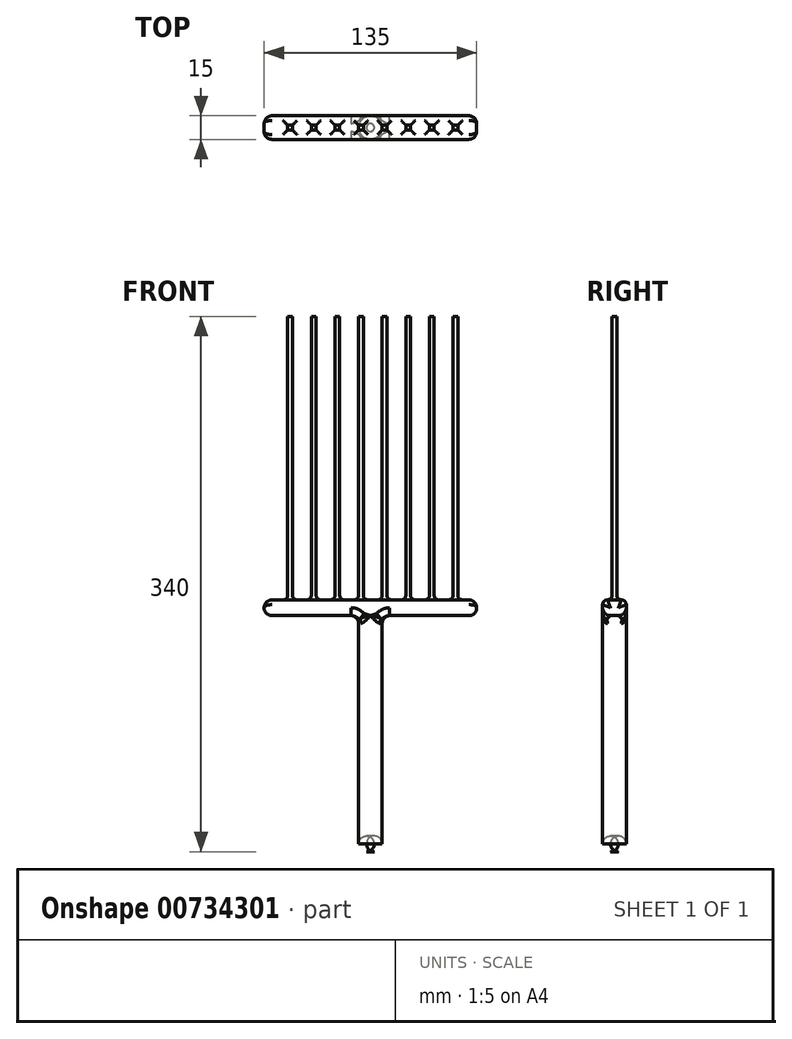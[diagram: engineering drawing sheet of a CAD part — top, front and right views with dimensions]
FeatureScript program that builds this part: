
annotation { "Feature Type Name" : "Feature", "Feature Type Description" : "" }
export const myFeature = defineFeature(function(context is Context, id is Id, definition is map)
    precondition{}
    {
        {
            var Q0;
            Q0=qCreatedBy(makeId("Top.planeOp"),FACE);
            var sketch = newSketch(context, id + "F0", { "sketchPlane" : qUnion([Q0])});
            skCircle(sketch, "E0", {"center": v(0, 0) * mm, "radius": 7.5 * mm});
            skSolve(sketch);
        }
        {
            var Q0;
            Q0 = qSketchRegion(id + "F0", true);
            extrude(context, id + "F1", {"entities" : qUnion([Q0]), "depth" : 150 * mm, "offsetDistance" : 25 * mm});
        }
        {
            var Q0;
            Q0=makeQuery(id+"F1.opExtrude","CAP_FACE",FACE,{"disambiguationData":[OSD([sQuery(id+"F0.wireOp",EDGE,"E0")])],"isStart":false});
            var sketch = newSketch(context, id + "F2", { "sketchPlane" : qUnion([Q0])});
            skLineSegment(sketch, "E1.bottom", {"start": v(67.5, -7.5) * mm, "end": v(-67.5, -7.5) * mm});
            skLineSegment(sketch, "E1.top", {"start": v(67.5, 7.5) * mm, "end": v(-67.5, 7.5) * mm});
            skLineSegment(sketch, "E1.left", {"start": v(67.5, -7.5) * mm, "end": v(67.5, 7.5) * mm});
            skLineSegment(sketch, "E1.right", {"start": v(-67.5, -7.5) * mm, "end": v(-67.5, 7.5) * mm});
            skPoint(sketch, "E1.middle", {"position": v(0, 0) * mm});
            skSolve(sketch);
        }
        {
            var Q0;
            Q0 = qSketchRegion(id + "F2", true);
            extrude(context, id + "F3", {"entities" : qUnion([Q0]), "operationType" : NewBodyOperationType.ADD, "depth" : 10 * mm, "offsetDistance" : 25 * mm});
        }
        {
            var Q0;
            Q0=makeQuery(id+"F3.opExtrude","CAP_FACE",FACE,{"disambiguationData":[OSD([sQuery(id+"F2.wireOp",EDGE,"E1.bottom"),sQuery(id+"F2.wireOp",EDGE,"E1.top"),sQuery(id+"F2.wireOp",EDGE,"E1.left"),sQuery(id+"F2.wireOp",EDGE,"E1.right")])],"isStart":false});
            var sketch = newSketch(context, id + "F4", { "sketchPlane" : qUnion([Q0])});
            skLineSegment(sketch, "E2.bottom", {"start": v(-64.5, -1.5) * mm, "end": v(-67.5, -1.5) * mm});
            skLineSegment(sketch, "E2.top", {"start": v(-64.5, 1.5) * mm, "end": v(-67.5, 1.5) * mm});
            skLineSegment(sketch, "E2.left", {"start": v(-64.5, -1.5) * mm, "end": v(-64.5, 1.5) * mm});
            skLineSegment(sketch, "E2.right", {"start": v(-67.5, -1.5) * mm, "end": v(-67.5, 1.5) * mm});
            skPoint(sketch, "E2.middle", {"position": v(-66, 0) * mm});
            skLineSegment(sketch, "E3.bottom", {"start": v(-49.5, -1.5) * mm, "end": v(-52.5, -1.5) * mm});
            skLineSegment(sketch, "E3.top", {"start": v(-49.5, 1.5) * mm, "end": v(-52.5, 1.5) * mm});
            skLineSegment(sketch, "E3.left", {"start": v(-49.5, -1.5) * mm, "end": v(-49.5, 1.5) * mm});
            skLineSegment(sketch, "E3.right", {"start": v(-52.5, -1.5) * mm, "end": v(-52.5, 1.5) * mm});
            skPoint(sketch, "E3.middle", {"position": v(-51, 0) * mm});
            skLineSegment(sketch, "E4.bottom", {"start": v(-34.5, -1.5) * mm, "end": v(-37.5, -1.5) * mm});
            skLineSegment(sketch, "E4.top", {"start": v(-34.5, 1.5) * mm, "end": v(-37.5, 1.5) * mm});
            skLineSegment(sketch, "E4.left", {"start": v(-34.5, -1.5) * mm, "end": v(-34.5, 1.5) * mm});
            skLineSegment(sketch, "E4.right", {"start": v(-37.5, -1.5) * mm, "end": v(-37.5, 1.5) * mm});
            skPoint(sketch, "E4.middle", {"position": v(-36, 0) * mm});
            skLineSegment(sketch, "E5.bottom", {"start": v(-19.5, -1.5) * mm, "end": v(-22.5, -1.5) * mm});
            skLineSegment(sketch, "E5.top", {"start": v(-19.5, 1.5) * mm, "end": v(-22.5, 1.5) * mm});
            skLineSegment(sketch, "E5.left", {"start": v(-19.5, -1.5) * mm, "end": v(-19.5, 1.5) * mm});
            skLineSegment(sketch, "E5.right", {"start": v(-22.5, -1.5) * mm, "end": v(-22.5, 1.5) * mm});
            skPoint(sketch, "E5.middle", {"position": v(-21, 0) * mm});
            skLineSegment(sketch, "E6.bottom", {"start": v(-4.5, -1.5) * mm, "end": v(-7.5, -1.5) * mm});
            skLineSegment(sketch, "E6.top", {"start": v(-4.5, 1.5) * mm, "end": v(-7.5, 1.5) * mm});
            skLineSegment(sketch, "E6.left", {"start": v(-4.5, -1.5) * mm, "end": v(-4.5, 1.5) * mm});
            skLineSegment(sketch, "E6.right", {"start": v(-7.5, -1.5) * mm, "end": v(-7.5, 1.5) * mm});
            skPoint(sketch, "E6.middle", {"position": v(-6, 0) * mm});
            skLineSegment(sketch, "E7.bottom", {"start": v(10.5, -1.5) * mm, "end": v(7.5, -1.5) * mm});
            skLineSegment(sketch, "E7.top", {"start": v(10.5, 1.5) * mm, "end": v(7.5, 1.5) * mm});
            skLineSegment(sketch, "E7.left", {"start": v(10.5, -1.5) * mm, "end": v(10.5, 1.5) * mm});
            skLineSegment(sketch, "E7.right", {"start": v(7.5, -1.5) * mm, "end": v(7.5, 1.5) * mm});
            skPoint(sketch, "E7.middle", {"position": v(9, 0) * mm});
            skLineSegment(sketch, "E8.bottom", {"start": v(25.5, -1.5) * mm, "end": v(22.5, -1.5) * mm});
            skLineSegment(sketch, "E8.top", {"start": v(25.5, 1.5) * mm, "end": v(22.5, 1.5) * mm});
            skLineSegment(sketch, "E8.left", {"start": v(25.5, -1.5) * mm, "end": v(25.5, 1.5) * mm});
            skLineSegment(sketch, "E8.right", {"start": v(22.5, -1.5) * mm, "end": v(22.5, 1.5) * mm});
            skPoint(sketch, "E8.middle", {"position": v(24, 0) * mm});
            skLineSegment(sketch, "E9.bottom", {"start": v(40.5, -1.5) * mm, "end": v(37.5, -1.5) * mm});
            skLineSegment(sketch, "E9.top", {"start": v(40.5, 1.5) * mm, "end": v(37.5, 1.5) * mm});
            skLineSegment(sketch, "E9.left", {"start": v(40.5, -1.5) * mm, "end": v(40.5, 1.5) * mm});
            skLineSegment(sketch, "E9.right", {"start": v(37.5, -1.5) * mm, "end": v(37.5, 1.5) * mm});
            skPoint(sketch, "E9.middle", {"position": v(39, 0) * mm});
            skLineSegment(sketch, "E10.bottom", {"start": v(55.5, -1.5) * mm, "end": v(52.5, -1.5) * mm});
            skLineSegment(sketch, "E10.top", {"start": v(55.5, 1.5) * mm, "end": v(52.5, 1.5) * mm});
            skLineSegment(sketch, "E10.left", {"start": v(55.5, -1.5) * mm, "end": v(55.5, 1.5) * mm});
            skLineSegment(sketch, "E10.right", {"start": v(52.5, -1.5) * mm, "end": v(52.5, 1.5) * mm});
            skPoint(sketch, "E10.middle", {"position": v(54, 0) * mm});
            skLineSegment(sketch, "E11.bottom", {"start": v(67.5, -1.5) * mm, "end": v(64.5, -1.5) * mm});
            skLineSegment(sketch, "E11.top", {"start": v(67.5, 1.5) * mm, "end": v(64.5, 1.5) * mm});
            skLineSegment(sketch, "E11.left", {"start": v(67.5, -1.5) * mm, "end": v(67.5, 1.5) * mm});
            skLineSegment(sketch, "E11.right", {"start": v(64.5, -1.5) * mm, "end": v(64.5, 1.5) * mm});
            skPoint(sketch, "E11.middle", {"position": v(66, 0) * mm});
            skSolve(sketch);
        }
        {
            var Q0;
            Q0 = qSketchRegion(id + "F4", true);
            extrude(context, id + "F5", {"entities" : qUnion([Q0]), "operationType" : NewBodyOperationType.ADD, "depth" : 180 * mm, "offsetDistance" : 25 * mm});
        }
        {
            var Q0;
            Q0=makeQuery(id+"F1.opExtrude","CAP_EDGE",EDGE,{"disambiguationData":[OSD([sQuery(id+"F0.wireOp",EDGE,"E0")])],"isStart":true});
            var Q1;
            Q1=makeQuery(id+"F1.opExtrude","SWEPT_FACE",FACE,{"disambiguationData":[OSD([sQuery(id+"F0.wireOp",EDGE,"E0")])]});
            fillet(context, id + "F6", {"entities" : qUnion([Q0, Q1]), "radius" : 5 * mm, "tangentPropagation" : true, "allowEdgeOverflow" : false});
        }
        {
            var Q0;
            {var subQ0=sQuery(id+"F2.wireOp",EDGE,"E1.top");var subQ1=sQuery(id+"F2.wireOp",EDGE,"E1.right");var subQ2=sQuery(id+"F2.wireOp",EDGE,"E1.bottom");var subQ3=makeQuery(id+"F3.opExtrude","CAP_FACE",FACE,{"disambiguationData":[OSD([subQ2,subQ0,sQuery(id+"F2.wireOp",EDGE,"E1.left"),subQ1])],"isStart":true});Q0=makeQuery(id+"F3.boolean.opBoolean","SPLIT",FACE,{"disambiguationData":[TD([makeQuery(id+"F3.opExtrude","SWEPT_FACE",FACE,{"disambiguationData":[OSD([subQ1])]})])],"derivedFrom":subQ3});}
            var Q1;
            {var subQ0=sQuery(id+"F2.wireOp",EDGE,"E1.top");var subQ1=sQuery(id+"F2.wireOp",EDGE,"E1.left");var subQ2=sQuery(id+"F2.wireOp",EDGE,"E1.bottom");var subQ3=makeQuery(id+"F3.opExtrude","CAP_FACE",FACE,{"disambiguationData":[OSD([subQ2,subQ0,subQ1,sQuery(id+"F2.wireOp",EDGE,"E1.right")])],"isStart":true});Q1=makeQuery(id+"F3.boolean.opBoolean","SPLIT",FACE,{"disambiguationData":[TD([makeQuery(id+"F3.opExtrude","SWEPT_FACE",FACE,{"disambiguationData":[OSD([subQ1])]})])],"derivedFrom":subQ3});}
            var Q2;
            Q2=makeQuery(id+"F5.boolean.opBoolean","MERGE",FACE,{"derivedFrom":[makeQuery(id+"F3.opExtrude","SWEPT_FACE",FACE,{"disambiguationData":[OSD([sQuery(id+"F2.wireOp",EDGE,"E1.left")])]}),makeQuery(id+"F5.opExtrude","SWEPT_FACE",FACE,{"disambiguationData":[OSD([sQuery(id+"F4.wireOp",EDGE,"E11.left")])]})]});
            var Q3;
            Q3=makeQuery(id+"F5.boolean.opBoolean","MERGE",FACE,{"derivedFrom":[makeQuery(id+"F3.opExtrude","SWEPT_FACE",FACE,{"disambiguationData":[OSD([sQuery(id+"F2.wireOp",EDGE,"E1.right")])]}),makeQuery(id+"F5.opExtrude","SWEPT_FACE",FACE,{"disambiguationData":[OSD([sQuery(id+"F4.wireOp",EDGE,"E2.right")])]})]});
            fillet(context, id + "F7", {"entities" : qUnion([Q0, Q1, Q2, Q3]), "radius" : 5 * mm, "tangentPropagation" : true, "allowEdgeOverflow" : false});
        }
        {
            var Q0;
            Q0=makeQuery(id+"F3.opExtrude","CAP_FACE",FACE,{"disambiguationData":[OSD([sQuery(id+"F2.wireOp",EDGE,"E1.bottom"),sQuery(id+"F2.wireOp",EDGE,"E1.top"),sQuery(id+"F2.wireOp",EDGE,"E1.left"),sQuery(id+"F2.wireOp",EDGE,"E1.right")])],"isStart":false});
            fillet(context, id + "F8", {"entities" : qUnion([Q0]), "radius" : 3 * mm, "tangentPropagation" : true, "allowEdgeOverflow" : false});
        }
    });
